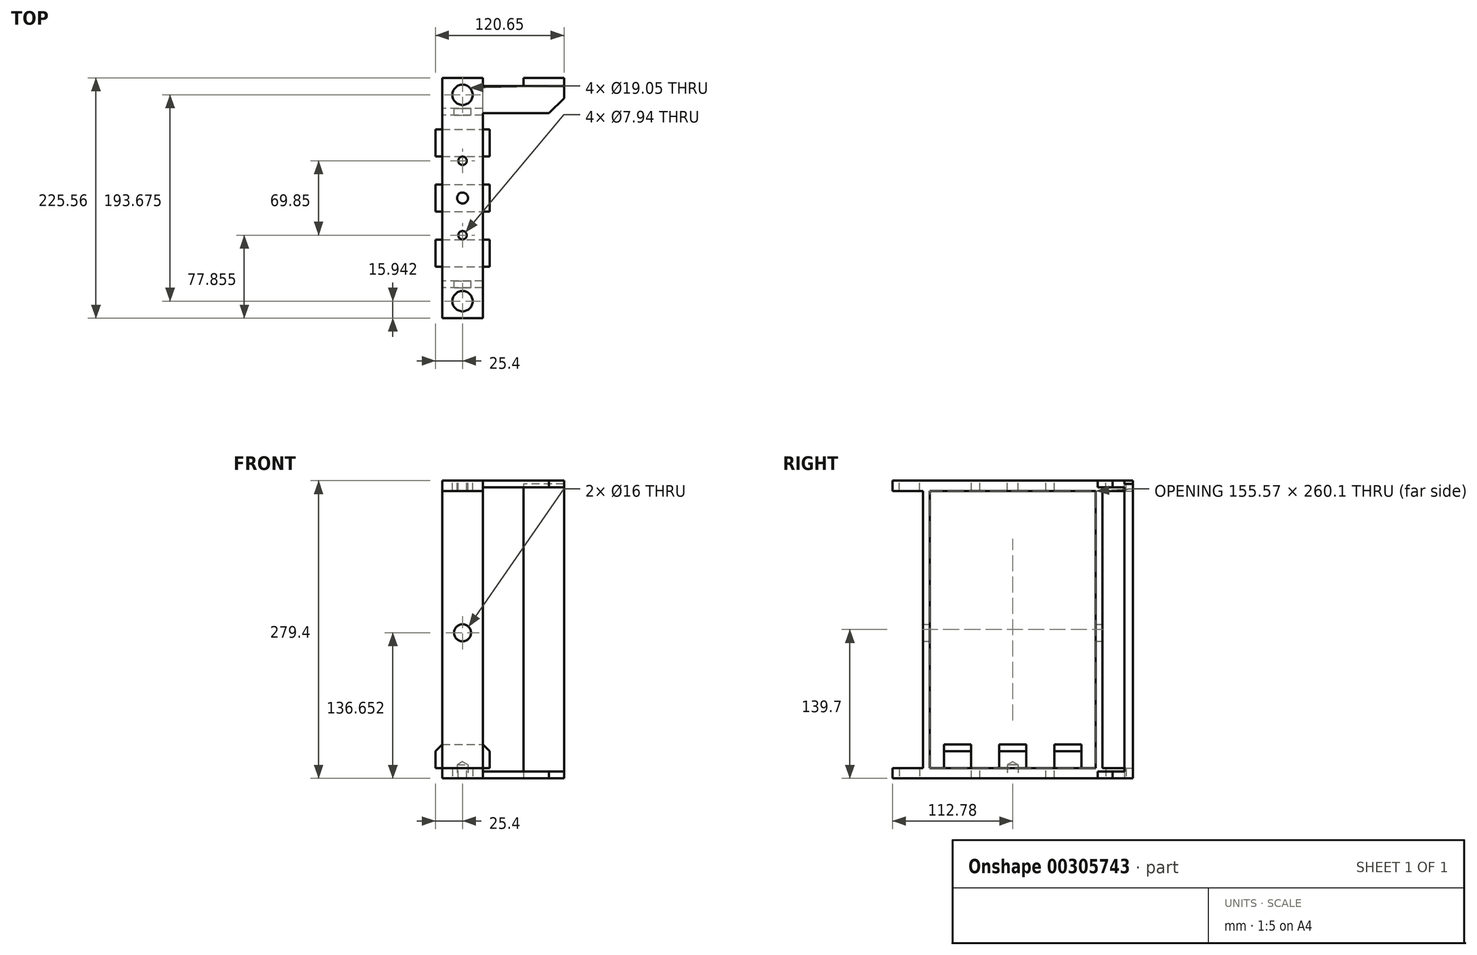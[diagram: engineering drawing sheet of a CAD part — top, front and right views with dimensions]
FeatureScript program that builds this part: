
annotation { "Feature Type Name" : "Feature", "Feature Type Description" : "" }
export const myFeature = defineFeature(function(context is Context, id is Id, definition is map)
    precondition{}
    {
        {
            var Q0;
            Q0=qCreatedBy(makeId("Right.planeOp"),FACE);
            var sketch = newSketch(context, id + "F0", { "sketchPlane" : qUnion([Q0])});
            skLineSegment(sketch, "E0.bottom", {"start": v(-112.78, 139.7) * mm, "end": v(112.78, 139.7) * mm, "construction": true});
            skLineSegment(sketch, "E0.top", {"start": v(-112.78, -139.7) * mm, "end": v(112.78, -139.7) * mm, "construction": true});
            skLineSegment(sketch, "E0.left", {"start": v(-112.78, 139.7) * mm, "end": v(-112.78, -139.7) * mm, "construction": true});
            skLineSegment(sketch, "E0.right", {"start": v(112.78, 139.7) * mm, "end": v(112.78, -139.7) * mm, "construction": true});
            skPoint(sketch, "E0.middle", {"position": v(0, 0) * mm});
            skLineSegment(sketch, "E1.bottom", {"start": v(-112.78, 139.7) * mm, "end": v(112.78, 139.7) * mm});
            skLineSegment(sketch, "E1.top", {"start": v(-112.78, 130.05) * mm, "end": v(112.78, 130.05) * mm});
            skLineSegment(sketch, "E1.left", {"start": v(-112.78, 139.7) * mm, "end": v(-112.78, 130.05) * mm});
            skLineSegment(sketch, "E1.right", {"start": v(112.78, 139.7) * mm, "end": v(112.78, 130.05) * mm});
            skLineSegment(sketch, "E2", {"start": v(-207.6, 0) * mm, "end": v(204.57, 0) * mm, "construction": true});
            skSolve(sketch);
        }
        {
            var Q0;
            Q0 = qSketchRegion(id + "F0", true);
            extrude(context, id + "F1", {"entities" : qUnion([Q0]), "endBound" : BoundingType.SYMMETRIC, "depth" : 38.1 * mm});
        }
        {
            var Q0;
            Q0=makeQuery(id+"F1.opExtrude","SWEPT_FACE",FACE,{"disambiguationData":[OSD([sQuery(id+"F0.wireOp",EDGE,"E1.bottom")])]});
            var sketch = newSketch(context, id + "F2", { "sketchPlane" : qUnion([Q0])});
            skLineSegment(sketch, "E3", {"start": v(0, -177.25) * mm, "end": v(0, 167.17) * mm, "construction": true});
            skLineSegment(sketch, "E4", {"start": v(-122.09, 0) * mm, "end": v(96.88, 0) * mm, "construction": true});
            skLineSegment(sketch, "E5.0", {"start": v(-122.09, -96.84) * mm, "end": v(96.88, -96.84) * mm, "construction": true});
            skPoint(sketch, "E6", {"position": v(0, -96.84) * mm});
            skPoint(sketch, "E7.MirrorP", {"position": v(0, 96.84) * mm});
            skSolve(sketch);
        }
        {
            var Q0;
            Q0=sQuery(id+"F2.wireOp",VERTEX,"E6");
            var Q1;
            Q1=sQuery(id+"F2.wireOp",VERTEX,"E7.MirrorP");
            var Q2;
            Q2=makeQuery(id+"F1.opExtrude","SWEPT_BODY",BODY,{"disambiguationData":[OSD([sQuery(id+"F0.wireOp",EDGE,"E1.bottom"),sQuery(id+"F0.wireOp",EDGE,"E1.top"),sQuery(id+"F0.wireOp",EDGE,"E1.left"),sQuery(id+"F0.wireOp",EDGE,"E1.right")])]});
            hole(context, id + "F3", {"style" : HoleStyle.SIMPLE, "endStyle" : HoleEndStyle.THROUGH, "holeDiameter" : 19.05 * mm, "tappedDepth" : 24.13 * mm, "tapClearance" : 3, "startFromSketch" : true, "locations" : qUnion([Q0, Q1]), "scope" : qUnion([Q2])});
        }
        {
            var Q0;
            Q0=makeQuery(id+"F1.opExtrude","SWEPT_BODY",BODY,{"disambiguationData":[OSD([sQuery(id+"F0.wireOp",EDGE,"E1.bottom"),sQuery(id+"F0.wireOp",EDGE,"E1.top"),sQuery(id+"F0.wireOp",EDGE,"E1.left"),sQuery(id+"F0.wireOp",EDGE,"E1.right")])]});
            var Q1;
            Q1=qCreatedBy(makeId("Top.planeOp"),FACE);
            mirror(context, id + "F4", {"entities" : qUnion([Q0]), "mirrorPlane" : qUnion([Q1])});
        }
        {
            var Q0;
            Q0=qCreatedBy(makeId("Right.planeOp"),FACE);
            var sketch = newSketch(context, id + "F5", { "sketchPlane" : qUnion([Q0])});
            skLineSegment(sketch, "E8", {"start": v(0, 150.78) * mm, "end": v(0, -158.23) * mm, "construction": true});
            skLineSegment(sketch, "E9.0", {"start": v(-77.79, 150.78) * mm, "end": v(-77.79, -158.23) * mm, "construction": true});
            skLineSegment(sketch, "E10.0", {"start": v(-112.78, 130.05) * mm, "end": v(112.78, 130.05) * mm, "construction": true});
            skLineSegment(sketch, "E11.0", {"start": v(-112.78, -130.05) * mm, "end": v(112.78, -130.05) * mm, "construction": true});
            skLineSegment(sketch, "E12.bottom", {"start": v(-77.79, 130.05) * mm, "end": v(-84.14, 130.05) * mm});
            skLineSegment(sketch, "E12.top", {"start": v(-77.79, -130.05) * mm, "end": v(-84.14, -130.05) * mm});
            skLineSegment(sketch, "E12.left", {"start": v(-77.79, 130.05) * mm, "end": v(-77.79, -130.05) * mm});
            skLineSegment(sketch, "E12.right", {"start": v(-84.14, 130.05) * mm, "end": v(-84.14, -130.05) * mm});
            skLineSegment(sketch, "E13.MirrorCS", {"start": v(77.79, 130.05) * mm, "end": v(84.14, 130.05) * mm});
            skLineSegment(sketch, "E14.MirrorCS", {"start": v(77.79, -130.05) * mm, "end": v(84.14, -130.05) * mm});
            skLineSegment(sketch, "E15.MirrorCS", {"start": v(77.79, 130.05) * mm, "end": v(77.79, -130.05) * mm});
            skLineSegment(sketch, "E16.MirrorCS", {"start": v(84.14, 130.05) * mm, "end": v(84.14, -130.05) * mm});
            skLineSegment(sketch, "E17.MirrorCS", {"start": v(77.79, 150.78) * mm, "end": v(77.79, -158.23) * mm, "construction": true});
            skSolve(sketch);
        }
        {
            var Q0;
            Q0 = qSketchRegion(id + "F5", true);
            extrude(context, id + "F6", {"entities" : qUnion([Q0]), "endBound" : BoundingType.SYMMETRIC, "depth" : 38.1 * mm});
        }
        {
            var Q0;
            Q0=makeQuery(id+"F6.opExtrude","SWEPT_FACE",FACE,{"disambiguationData":[OSD([sQuery(id+"F5.wireOp",EDGE,"E16.MirrorCS")])]});
            var sketch = newSketch(context, id + "F7", { "sketchPlane" : qUnion([Q0])});
            skLineSegment(sketch, "E18.0", {"start": v(-92.9, -130.05) * mm, "end": v(19.05, -130.05) * mm, "construction": true});
            skPoint(sketch, "E19.orphan", {"position": v(-19.05, -130.05) * mm});
            skLineSegment(sketch, "E20", {"start": v(0, 168.5) * mm, "end": v(0, -166.5) * mm, "construction": true});
            skLineSegment(sketch, "E21.0", {"start": v(-92.9, -3.05) * mm, "end": v(19.05, -3.05) * mm, "construction": true});
            skPoint(sketch, "E22", {"position": v(0, -3.05) * mm});
            skSolve(sketch);
        }
        {
            var Q0;
            Q0=makeQuery(id+"F1.opExtrude","SWEPT_BODY",BODY,{"disambiguationData":[OSD([sQuery(id+"F0.wireOp",EDGE,"E1.bottom"),sQuery(id+"F0.wireOp",EDGE,"E1.top"),sQuery(id+"F0.wireOp",EDGE,"E1.left"),sQuery(id+"F0.wireOp",EDGE,"E1.right")])]});
            var Q1;
            Q1=makeQuery(id+"F6.opExtrude","SWEPT_BODY",BODY,{"disambiguationData":[OSD([sQuery(id+"F5.wireOp",EDGE,"E12.bottom"),sQuery(id+"F5.wireOp",EDGE,"E12.top"),sQuery(id+"F5.wireOp",EDGE,"E12.left"),sQuery(id+"F5.wireOp",EDGE,"E12.right")])]});
            var Q2;
            Q2=makeQuery(id+"F6.opExtrude","SWEPT_BODY",BODY,{"disambiguationData":[OSD([sQuery(id+"F5.wireOp",EDGE,"E13.MirrorCS"),sQuery(id+"F5.wireOp",EDGE,"E14.MirrorCS"),sQuery(id+"F5.wireOp",EDGE,"E15.MirrorCS"),sQuery(id+"F5.wireOp",EDGE,"E16.MirrorCS")])]});
            var Q3;
            Q3=makeQuery(id+"F4.opPattern","COPY",BODY,{"derivedFrom":makeQuery(id+"F1.opExtrude","SWEPT_BODY",BODY,{"disambiguationData":[OSD([sQuery(id+"F0.wireOp",EDGE,"E1.bottom"),sQuery(id+"F0.wireOp",EDGE,"E1.top"),sQuery(id+"F0.wireOp",EDGE,"E1.left"),sQuery(id+"F0.wireOp",EDGE,"E1.right")])]}),"instanceName":"1"});
            booleanBodies(context, id + "F8", {"operationType" : BooleanOperationType.UNION, "tools" : qUnion([Q0, Q1, Q2, Q3])});
        }
        {
            var Q0;
            Q0=sQuery(id+"F7.wireOp",VERTEX,"E22");
            var Q1;
            Q1=makeQuery(id+"F1.opExtrude","SWEPT_BODY",BODY,{"disambiguationData":[OSD([sQuery(id+"F0.wireOp",EDGE,"E1.bottom"),sQuery(id+"F0.wireOp",EDGE,"E1.top"),sQuery(id+"F0.wireOp",EDGE,"E1.left"),sQuery(id+"F0.wireOp",EDGE,"E1.right")])]});
            hole(context, id + "F9", {"style" : HoleStyle.SIMPLE, "endStyle" : HoleEndStyle.THROUGH, "holeDiameter" : 16 * mm, "tappedDepth" : 24.13 * mm, "tapClearance" : 3, "startFromSketch" : true, "locations" : qUnion([Q0]), "scope" : qUnion([Q1])});
        }
        {
            var Q0;
            {var subQ2=sQuery(id+"F0.wireOp",EDGE,"E1.top");var subQ7=sQuery(id+"F5.wireOp",EDGE,"E12.left");Q0=makeQuery(id+"F8.opBoolean","SPLIT",FACE,{"disambiguationData":[TD([makeQuery(id+"F6.opExtrude","SWEPT_FACE",FACE,{"disambiguationData":[OSD([subQ7])]})])],"derivedFrom":makeQuery(id+"F4.opPattern","COPY",FACE,{"derivedFrom":makeQuery(id+"F1.opExtrude","SWEPT_FACE",FACE,{"disambiguationData":[OSD([subQ2])]}),"instanceName":"1"})});}
            var sketch = newSketch(context, id + "F10", { "sketchPlane" : qUnion([Q0])});
            skLineSegment(sketch, "E23", {"start": v(-127.69, 0) * mm, "end": v(108.08, 0) * mm, "construction": true});
            skLineSegment(sketch, "E24", {"start": v(0, -187.89) * mm, "end": v(0, 187.89) * mm, "construction": true});
            skLineSegment(sketch, "E25.0", {"start": v(-127.69, -51.69) * mm, "end": v(108.08, -51.69) * mm, "construction": true});
            skLineSegment(sketch, "E26.bottom", {"start": v(-25.4, -64.39) * mm, "end": v(25.4, -64.39) * mm});
            skLineSegment(sketch, "E26.top", {"start": v(-25.4, -38.99) * mm, "end": v(25.4, -38.99) * mm});
            skLineSegment(sketch, "E26.left", {"start": v(-25.4, -64.39) * mm, "end": v(-25.4, -38.99) * mm});
            skLineSegment(sketch, "E26.right", {"start": v(25.4, -64.39) * mm, "end": v(25.4, -38.99) * mm});
            skPoint(sketch, "E26.middle", {"position": v(0, -51.69) * mm});
            skLineSegment(sketch, "E27.0.1.0", {"start": v(-25.4, -12.7) * mm, "end": v(25.4, -12.7) * mm});
            skLineSegment(sketch, "E27.0.1.1", {"start": v(-25.4, 12.7) * mm, "end": v(25.4, 12.7) * mm});
            skLineSegment(sketch, "E27.0.1.2", {"start": v(-25.4, -12.7) * mm, "end": v(-25.4, 12.7) * mm});
            skLineSegment(sketch, "E27.0.1.3", {"start": v(25.4, -12.7) * mm, "end": v(25.4, 12.7) * mm});
            skPoint(sketch, "E27.0.1.4", {"position": v(0, 0) * mm});
            skLineSegment(sketch, "E27.0.2.0", {"start": v(-25.4, 38.99) * mm, "end": v(25.4, 38.99) * mm});
            skLineSegment(sketch, "E27.0.2.1", {"start": v(-25.4, 64.39) * mm, "end": v(25.4, 64.39) * mm});
            skLineSegment(sketch, "E27.0.2.2", {"start": v(-25.4, 38.99) * mm, "end": v(-25.4, 64.39) * mm});
            skLineSegment(sketch, "E27.0.2.3", {"start": v(25.4, 38.99) * mm, "end": v(25.4, 64.39) * mm});
            skPoint(sketch, "E27.0.2.4", {"position": v(0, 51.69) * mm});
            skLineSegment(sketch, "E27.direction1", {"start": v(-25.4, -64.39) * mm, "end": v(0, -64.39) * mm, "construction": true});
            skLineSegment(sketch, "E27.direction2", {"start": v(-25.4, -64.39) * mm, "end": v(-25.4, -12.7) * mm, "construction": true});
            skSolve(sketch);
        }
        {
            var Q0;
            Q0 = qSketchRegion(id + "F10", true);
            extrude(context, id + "F11", {"entities" : qUnion([Q0]), "operationType" : NewBodyOperationType.ADD, "depth" : 22.35 * mm});
        }
        {
            var Q0;
            Q0=makeQuery(id+"F11.opExtrude","CAP_EDGE",EDGE,{"disambiguationData":[OSD([sQuery(id+"F10.wireOp",EDGE,"E26.left")])],"isStart":false});
            var Q1;
            Q1=makeQuery(id+"F11.opExtrude","CAP_EDGE",EDGE,{"disambiguationData":[OSD([sQuery(id+"F10.wireOp",EDGE,"E27.0.1.2")])],"isStart":false});
            var Q2;
            Q2=makeQuery(id+"F11.opExtrude","CAP_EDGE",EDGE,{"disambiguationData":[OSD([sQuery(id+"F10.wireOp",EDGE,"E27.0.2.2")])],"isStart":false});
            var Q3;
            Q3=makeQuery(id+"F11.opExtrude","CAP_EDGE",EDGE,{"disambiguationData":[OSD([sQuery(id+"F10.wireOp",EDGE,"E27.0.2.3")])],"isStart":false});
            var Q4;
            Q4=makeQuery(id+"F11.opExtrude","CAP_EDGE",EDGE,{"disambiguationData":[OSD([sQuery(id+"F10.wireOp",EDGE,"E27.0.1.3")])],"isStart":false});
            var Q5;
            Q5=makeQuery(id+"F11.opExtrude","CAP_EDGE",EDGE,{"disambiguationData":[OSD([sQuery(id+"F10.wireOp",EDGE,"E26.right")])],"isStart":false});
            chamfer(context, id + "F12", {"entities" : qUnion([Q0, Q1, Q2, Q3, Q4, Q5]), "width" : 6.35 * mm, "tangentPropagation" : true});
        }
        {
            var Q0;
            Q0=makeQuery(id+"F1.opExtrude","SWEPT_FACE",FACE,{"disambiguationData":[OSD([sQuery(id+"F0.wireOp",EDGE,"E1.bottom")])]});
            var sketch = newSketch(context, id + "F13", { "sketchPlane" : qUnion([Q0])});
            skLineSegment(sketch, "E28", {"start": v(-115.37, 0) * mm, "end": v(101.92, 0) * mm, "construction": true});
            skLineSegment(sketch, "E29", {"start": v(0, -161.57) * mm, "end": v(0, 180.6) * mm, "construction": true});
            skLineSegment(sketch, "E30.0", {"start": v(-115.37, -34.93) * mm, "end": v(101.92, -34.92) * mm, "construction": true});
            skPoint(sketch, "E31", {"position": v(0, -34.93) * mm});
            skPoint(sketch, "E32.MirrorP", {"position": v(0, 34.93) * mm});
            skSolve(sketch);
        }
        {
            var Q0;
            Q0=sQuery(id+"F13.wireOp",VERTEX,"E31");
            var Q1;
            Q1=sQuery(id+"F13.wireOp",VERTEX,"E32.MirrorP");
            var Q2;
            Q2=makeQuery(id+"F1.opExtrude","SWEPT_BODY",BODY,{"disambiguationData":[OSD([sQuery(id+"F0.wireOp",EDGE,"E1.bottom"),sQuery(id+"F0.wireOp",EDGE,"E1.top"),sQuery(id+"F0.wireOp",EDGE,"E1.left"),sQuery(id+"F0.wireOp",EDGE,"E1.right")])]});
            hole(context, id + "F14", {"style" : HoleStyle.SIMPLE, "endStyle" : HoleEndStyle.THROUGH, "standardTappedOrClearance" : lookupTablePath({ "standard" : "ANSI", "engagement" : "75%", "pitch" : "16 tpi", "size" : "3/8", "type" : "Tapped" }), "standardBlindInLast" : lookupTablePath({ "standard" : "ANSI", "engagement" : "75%", "pitch" : "16 tpi", "size" : "3/8", "type" : "Tapped" }), "holeDiameter" : 7.94 * mm, "showTappedDepth" : true, "tappedDepth" : 24.13 * mm, "tapClearance" : 3, "startFromSketch" : true, "locations" : qUnion([Q0, Q1]), "scope" : qUnion([Q2]), "majorDiameter" : 9.53 * mm});
        }
        {
            var Q0;
            Q0=makeQuery(id+"F1.opExtrude","SWEPT_FACE",FACE,{"disambiguationData":[OSD([sQuery(id+"F0.wireOp",EDGE,"E1.bottom")])]});
            var sketch = newSketch(context, id + "F15", { "sketchPlane" : qUnion([Q0])});
            skPoint(sketch, "E33", {"position": v(0, 0) * mm});
            skSolve(sketch);
        }
        {
            var Q0;
            Q0=sQuery(id+"F15.wireOp",VERTEX,"E33");
            var Q1;
            Q1=makeQuery(id+"F1.opExtrude","SWEPT_BODY",BODY,{"disambiguationData":[OSD([sQuery(id+"F0.wireOp",EDGE,"E1.bottom"),sQuery(id+"F0.wireOp",EDGE,"E1.top"),sQuery(id+"F0.wireOp",EDGE,"E1.left"),sQuery(id+"F0.wireOp",EDGE,"E1.right")])]});
            hole(context, id + "F16", {"style" : HoleStyle.SIMPLE, "endStyle" : HoleEndStyle.BLIND, "holeDiameter" : 10.3 * mm, "holeDepth" : 28.9 * mm, "tappedDepth" : 24.13 * mm, "tapClearance" : 3, "startFromSketch" : true, "locations" : qUnion([Q0]), "scope" : qUnion([Q1])});
        }
        {
            var Q0;
            Q0=makeQuery(id+"F4.opPattern","COPY",FACE,{"derivedFrom":makeQuery(id+"F1.opExtrude","SWEPT_FACE",FACE,{"disambiguationData":[OSD([sQuery(id+"F0.wireOp",EDGE,"E1.bottom")])]}),"instanceName":"1"});
            var sketch = newSketch(context, id + "F17", { "sketchPlane" : qUnion([Q0])});
            skPoint(sketch, "E34", {"position": v(0, 0) * mm});
            skSolve(sketch);
        }
        {
            var Q0;
            Q0=sQuery(id+"F17.wireOp",VERTEX,"E34");
            var Q1;
            Q1=makeQuery(id+"F1.opExtrude","SWEPT_BODY",BODY,{"disambiguationData":[OSD([sQuery(id+"F0.wireOp",EDGE,"E1.bottom"),sQuery(id+"F0.wireOp",EDGE,"E1.top"),sQuery(id+"F0.wireOp",EDGE,"E1.left"),sQuery(id+"F0.wireOp",EDGE,"E1.right")])]});
            hole(context, id + "F18", {"style" : HoleStyle.SIMPLE, "endStyle" : HoleEndStyle.BLIND, "holeDiameter" : 10.3 * mm, "holeDepth" : 12.7 * mm, "tappedDepth" : 24.13 * mm, "tapClearance" : 3, "startFromSketch" : true, "locations" : qUnion([Q0]), "scope" : qUnion([Q1])});
        }
        {
            var Q0;
            Q0=makeQuery(id+"F1.opExtrude","SWEPT_FACE",FACE,{"disambiguationData":[OSD([sQuery(id+"F0.wireOp",EDGE,"E1.bottom")])]});
            var sketch = newSketch(context, id + "F19", { "sketchPlane" : qUnion([Q0])});
            skLineSegment(sketch, "E35", {"start": v(-19.05, 112.78) * mm, "end": v(73.29, 112.78) * mm, "construction": true});
            skLineSegment(sketch, "E36.0", {"start": v(-19.05, 104.9) * mm, "end": v(73.29, 104.9) * mm, "construction": true});
            skLineSegment(sketch, "E37.0", {"start": v(-19.05, 79.5) * mm, "end": v(73.29, 79.5) * mm});
            skLineSegment(sketch, "E38.0", {"start": v(19.05, -112.78) * mm, "end": v(19.05, 112.78) * mm, "construction": true});
            skLineSegment(sketch, "E39.bottom", {"start": v(19.05, 79.5) * mm, "end": v(95.25, 79.5) * mm});
            skLineSegment(sketch, "E39.top", {"start": v(19.05, 104.9) * mm, "end": v(95.25, 104.9) * mm});
            skLineSegment(sketch, "E39.left", {"start": v(19.05, 79.5) * mm, "end": v(19.05, 104.9) * mm});
            skLineSegment(sketch, "E39.right", {"start": v(95.25, 79.5) * mm, "end": v(95.25, 104.9) * mm});
            skSolve(sketch);
        }
        {
            var Q0;
            Q0 = qSketchRegion(id + "F19", true);
            extrude(context, id + "F20", {"entities" : qUnion([Q0]), "oppositeDirection" : true, "depth" : 6.35 * mm});
        }
        {
            var Q0;
            Q0=makeQuery(id+"F20.opExtrude","SWEPT_BODY",BODY,{"disambiguationData":[OSD([sQuery(id+"F19.wireOp",EDGE,"E39.bottom"),sQuery(id+"F19.wireOp",EDGE,"E39.top"),sQuery(id+"F19.wireOp",EDGE,"E39.left"),sQuery(id+"F19.wireOp",EDGE,"E39.right")])]});
            var Q1;
            Q1=qCreatedBy(makeId("Top.planeOp"),FACE);
            mirror(context, id + "F21", {"operationType" : NewBodyOperationType.ADD, "entities" : qUnion([Q0]), "mirrorPlane" : qUnion([Q1])});
        }
        {
            var Q0;
            Q0=makeQuery(id+"F20.opExtrude","SWEPT_EDGE",EDGE,{"disambiguationData":[OSD([sQuery(id+"F19.wireOp",EDGE,"E39.bottom"),sQuery(id+"F19.wireOp",EDGE,"E39.right")])]});
            var Q1;
            Q1=makeQuery(id+"F21.opPattern","COPY",EDGE,{"derivedFrom":makeQuery(id+"F20.opExtrude","SWEPT_EDGE",EDGE,{"disambiguationData":[OSD([sQuery(id+"F19.wireOp",EDGE,"E39.bottom"),sQuery(id+"F19.wireOp",EDGE,"E39.right")])]}),"instanceName":"1"});
            chamfer(context, id + "F22", {"entities" : qUnion([Q0, Q1]), "width" : 14.22 * mm, "tangentPropagation" : true});
        }
        {
            var Q0;
            Q0=makeQuery(id+"F21.opPattern","COPY",FACE,{"derivedFrom":makeQuery(id+"F20.opExtrude","SWEPT_FACE",FACE,{"disambiguationData":[OSD([sQuery(id+"F19.wireOp",EDGE,"E39.top")])]}),"instanceName":"1"});
            var sketch = newSketch(context, id + "F23", { "sketchPlane" : qUnion([Q0])});
            skLineSegment(sketch, "E40.0", {"start": v(-19.05, -139.7) * mm, "end": v(-95.25, -139.7) * mm, "construction": true});
            skLineSegment(sketch, "E41.0", {"start": v(-19.05, 139.7) * mm, "end": v(-95.25, 139.7) * mm, "construction": true});
            skLineSegment(sketch, "E42.bottom", {"start": v(-95.25, 136.53) * mm, "end": v(-57.15, 136.53) * mm});
            skLineSegment(sketch, "E42.top", {"start": v(-95.25, -139.7) * mm, "end": v(-57.15, -139.7) * mm});
            skLineSegment(sketch, "E42.left", {"start": v(-95.25, 136.53) * mm, "end": v(-95.25, -139.7) * mm});
            skLineSegment(sketch, "E42.right", {"start": v(-57.15, 136.53) * mm, "end": v(-57.15, -139.7) * mm});
            skSolve(sketch);
        }
        {
            var Q0;
            Q0 = qSketchRegion(id + "F23", true);
            extrude(context, id + "F24", {"entities" : qUnion([Q0]), "operationType" : NewBodyOperationType.ADD, "depth" : 7.87 * mm});
        }
    });
